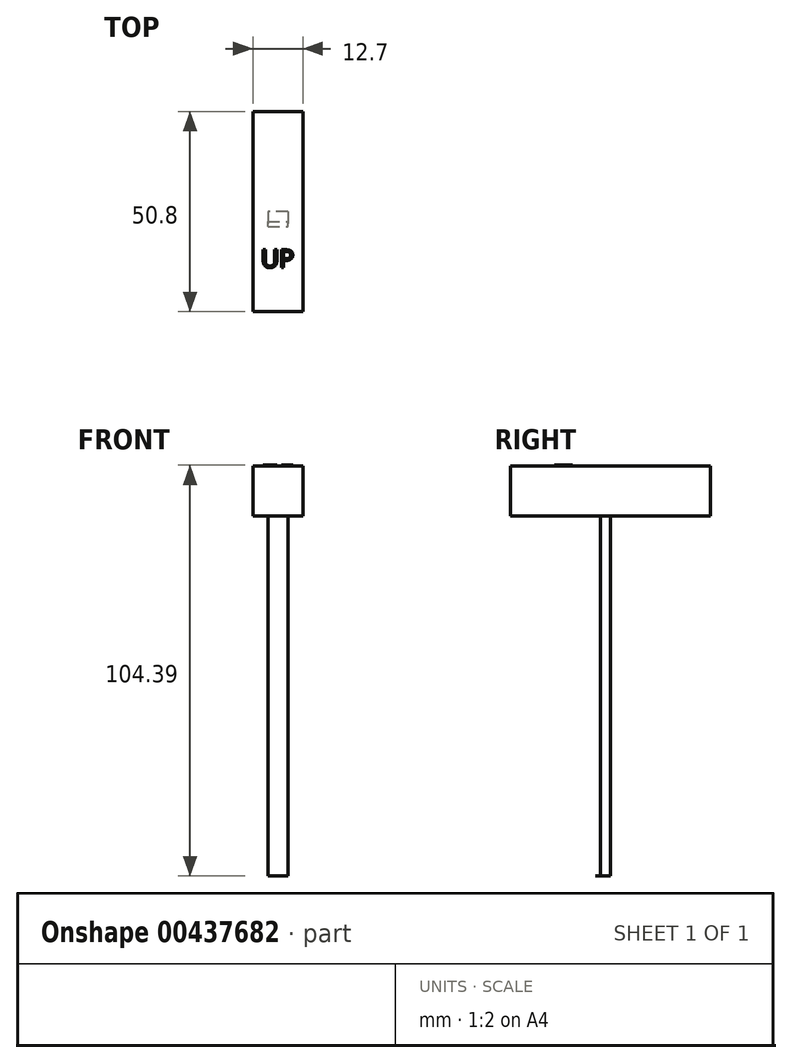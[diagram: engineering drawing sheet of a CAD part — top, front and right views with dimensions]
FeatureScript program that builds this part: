
annotation { "Feature Type Name" : "Feature", "Feature Type Description" : "" }
export const myFeature = defineFeature(function(context is Context, id is Id, definition is map)
    precondition{}
    {
        {
            var Q0;
            Q0=qCreatedBy(makeId("Front.planeOp"),FACE);
            var sketch = newSketch(context, id + "F0", { "sketchPlane" : qUnion([Q0])});
            skLineSegment(sketch, "E0.bottom", {"start": v(-6.35, 6.35) * mm, "end": v(6.35, 6.35) * mm});
            skLineSegment(sketch, "E0.top", {"start": v(-6.35, -6.35) * mm, "end": v(6.35, -6.35) * mm});
            skLineSegment(sketch, "E0.left", {"start": v(-6.35, 6.35) * mm, "end": v(-6.35, -6.35) * mm});
            skLineSegment(sketch, "E0.right", {"start": v(6.35, 6.35) * mm, "end": v(6.35, -6.35) * mm});
            skPoint(sketch, "E0.middle", {"position": v(0, 0) * mm});
            skSolve(sketch);
        }
        {
            var Q0;
            Q0=makeQuery(id+"F0.imprint","IMPRINT",FACE,{"disambiguationData":[TD([[makeQuery(id+"F0.imprint","IMPRINT",EDGE,{"derivedFrom":sQuery(id+"F0.wireOp",EDGE,"E0.bottom")}),-1.0]])]});
            extrude(context, id + "F1", {"entities" : qUnion([Q0]), "oppositeDirection" : true, "depth" : 50.8 * mm});
        }
        {
            var Q0;
            Q0=makeQuery(id+"F1.opExtrude","SWEPT_FACE",FACE,{"disambiguationData":[OSD([sQuery(id+"F0.wireOp",EDGE,"E0.right")])]});
            var sketch = newSketch(context, id + "F2", { "sketchPlane" : qUnion([Q0])});
            skLineSegment(sketch, "E1.bottom", {"start": v(25.4, 0) * mm, "end": v(-25.4, 0) * mm});
            skLineSegment(sketch, "E1.top", {"start": v(25.4, 12.7) * mm, "end": v(-25.4, 12.7) * mm});
            skLineSegment(sketch, "E1.left", {"start": v(25.4, 0) * mm, "end": v(25.4, 12.7) * mm});
            skLineSegment(sketch, "E1.right", {"start": v(-25.4, 0) * mm, "end": v(-25.4, 12.7) * mm});
            skPoint(sketch, "E1.middle", {"position": v(0, 6.35) * mm});
            skSolve(sketch);
        }
        {
            var Q0;
            {var subQ2=sQuery(id+"F2.wireOp",EDGE,"E1.top");Q0=makeQuery(id+"F2.imprint","IMPRINT",FACE,{"disambiguationData":[TD([[makeQuery(id+"F2.imprint","IMPRINT",EDGE,{"derivedFrom":subQ2}),1.0]])]});}
            var Q1;
            {var subQ0=sQuery(id+"F2.wireOp",EDGE,"E1.left");var subQ1=sQuery(id+"F2.wireOp",EDGE,"E1.bottom");var subQ2=makeQuery(id+"F2.imprint","INTERSECT",VERTEX,{"derivedFrom":[subQ1,subQ0]});Q1=makeQuery(id+"F2.imprint","IMPRINT",FACE,{"disambiguationData":[TD([[makeQuery(id+"F2.imprint","IMPRINT",EDGE,{"disambiguationData":[TD([[subQ2,-1.0]])],"derivedFrom":subQ1}),-1.0]])]});}
            extrude(context, id + "F3", {"entities" : qUnion([Q0, Q1]), "operationType" : NewBodyOperationType.REMOVE, "oppositeDirection" : true, "depth" : 25.4 * mm});
        }
        {
            var Q0;
            Q0=makeQuery(id+"F3.boolean.opBoolean","COPY",FACE,{"derivedFrom":makeQuery(id+"F3.opExtrude","SWEPT_FACE",FACE,{"disambiguationData":[OSD([sQuery(id+"F2.wireOp",EDGE,"E1.bottom")])]})});
            var sketch = newSketch(context, id + "F4", { "sketchPlane" : qUnion([Q0])});
            skLineSegment(sketch, "E2.bottom", {"start": v(-2.54, 22.86) * mm, "end": v(2.54, 22.86) * mm});
            skLineSegment(sketch, "E2.top", {"start": v(-2.54, 27.94) * mm, "end": v(2.54, 27.94) * mm});
            skLineSegment(sketch, "E2.left", {"start": v(-2.54, 22.86) * mm, "end": v(-2.54, 27.94) * mm});
            skLineSegment(sketch, "E2.right", {"start": v(2.54, 22.86) * mm, "end": v(2.54, 27.94) * mm});
            skPoint(sketch, "E2.middle", {"position": v(0, 25.4) * mm});
            skSolve(sketch);
        }
        {
            var Q0;
            {var subQ0=sQuery(id+"F4.wireOp",EDGE,"E2.bottom");Q0=makeQuery(id+"F4.imprint","IMPRINT",FACE,{"disambiguationData":[TD([[makeQuery(id+"F4.imprint","IMPRINT",EDGE,{"derivedFrom":subQ0}),1.0]])]});}
            extrude(context, id + "F5", {"entities" : qUnion([Q0]), "operationType" : NewBodyOperationType.REMOVE, "oppositeDirection" : true, "depth" : 25.4 * mm});
        }
        {
            var Q0;
            Q0=makeQuery(id+"F1.opExtrude","SWEPT_FACE",FACE,{"disambiguationData":[OSD([sQuery(id+"F0.wireOp",EDGE,"E0.right")])]});
            var sketch = newSketch(context, id + "F6", { "sketchPlane" : qUnion([Q0])});
            skLineSegment(sketch, "E3.bottom", {"start": v(25.4, 0) * mm, "end": v(0, 0) * mm});
            skLineSegment(sketch, "E3.top", {"start": v(25.4, 6.35) * mm, "end": v(0, 6.35) * mm});
            skLineSegment(sketch, "E3.left", {"start": v(25.4, 0) * mm, "end": v(25.4, 6.35) * mm});
            skLineSegment(sketch, "E3.right", {"start": v(0, 0) * mm, "end": v(0, 6.35) * mm});
            skSolve(sketch);
        }
        {
            var Q0;
            Q0=makeQuery(id+"F6.imprint","IMPRINT",FACE,{"disambiguationData":[TD([[makeQuery(id+"F6.imprint","IMPRINT",EDGE,{"derivedFrom":sQuery(id+"F6.wireOp",EDGE,"E3.bottom")}),-1.0]])]});
            extrude(context, id + "F7", {"entities" : qUnion([Q0]), "oppositeDirection" : true, "depth" : 12.7 * mm});
        }
        {
            var Q0;
            Q0=makeQuery(id+"F7.opExtrude","SWEPT_FACE",FACE,{"disambiguationData":[OSD([sQuery(id+"F6.wireOp",EDGE,"E3.bottom")])]});
            var sketch = newSketch(context, id + "F8", { "sketchPlane" : qUnion([Q0])});
            skLineSegment(sketch, "E4.bottom", {"start": v(-2.54, -25.4) * mm, "end": v(2.54, -25.4) * mm});
            skLineSegment(sketch, "E4.top", {"start": v(-2.54, -22.86) * mm, "end": v(2.54, -22.86) * mm});
            skLineSegment(sketch, "E4.left", {"start": v(-2.54, -25.4) * mm, "end": v(-2.54, -22.86) * mm});
            skLineSegment(sketch, "E4.right", {"start": v(2.54, -25.4) * mm, "end": v(2.54, -22.86) * mm});
            skLineSegment(sketch, "E5.top", {"start": v(-1.27, -25.4) * mm, "end": v(1.27, -25.4) * mm});
            skPoint(sketch, "E5.middle", {"position": v(0, -22.86) * mm});
            skSolve(sketch);
        }
        {
            var Q0;
            Q0=makeQuery(id+"F8.imprint","IMPRINT",FACE,{"disambiguationData":[TD([[makeQuery(id+"F8.imprint","IMPRINT",EDGE,{"derivedFrom":sQuery(id+"F8.wireOp",EDGE,"E4.bottom")}),1.0]])]});
            extrude(context, id + "F9", {"entities" : qUnion([Q0]), "operationType" : NewBodyOperationType.ADD, "depth" : 97.8 * mm});
        }
        {
            var Q0;
            Q0=makeQuery(id+"F9.opExtrude","CAP_FACE",FACE,{"disambiguationData":[OSD([sQuery(id+"F8.wireOp",EDGE,"E4.bottom"),sQuery(id+"F8.wireOp",EDGE,"E4.top"),sQuery(id+"F8.wireOp",EDGE,"E4.left"),sQuery(id+"F8.wireOp",EDGE,"E4.right"),sQuery(id+"F8.wireOp",EDGE,"E5.top")])],"isStart":false});
            var sketch = newSketch(context, id + "F10", { "sketchPlane" : qUnion([Q0])});
            skLineSegment(sketch, "E6.bottom", {"start": v(-2.54, -21.6) * mm, "end": v(2.54, -21.6) * mm});
            skLineSegment(sketch, "E6.top", {"start": v(-2.54, -24) * mm, "end": v(2.54, -24) * mm});
            skLineSegment(sketch, "E6.left", {"start": v(-2.54, -21.6) * mm, "end": v(-2.54, -24) * mm});
            skLineSegment(sketch, "E6.right", {"start": v(2.54, -21.6) * mm, "end": v(2.54, -24) * mm});
            skPoint(sketch, "E6.middle", {"position": v(0, -22.8) * mm});
            skPoint(sketch, "E6.middle.positionSnap0", {"position": v(0, -22.86) * mm});
            skPoint(sketch, "E6.centerSnap0", {"position": v(0, -22.86) * mm});
            skSolve(sketch);
        }
        {
            var Q0;
            {var subQ0=sQuery(id+"F10.wireOp",EDGE,"E6.bottom");Q0=makeQuery(id+"F10.imprint","IMPRINT",FACE,{"disambiguationData":[TD([[makeQuery(id+"F10.imprint","IMPRINT",EDGE,{"derivedFrom":subQ0}),-1.0]])]});}
            extrude(context, id + "F11", {"entities" : qUnion([Q0]), "operationType" : NewBodyOperationType.ADD, "oppositeDirection" : true, "depth" : 0.03 * mm});
        }
        {
            var Q0;
            Q0=makeQuery(id+"F7.opExtrude","SWEPT_FACE",FACE,{"disambiguationData":[OSD([sQuery(id+"F6.wireOp",EDGE,"E3.top")])]});
            var sketch = newSketch(context, id + "F12", { "sketchPlane" : qUnion([Q0])});
            skText(sketch, "E7", { "text": "UP\n", "fontName": "OpenSans-Regular.ttf"});
            const initialGuessF12  = {"E7": [-0.0043, 0.0112, 1, 0, 0.00455]};
            skSetInitialGuess(sketch, initialGuessF12);
            skSolve(sketch);
        }
        {
            var Q0;
            Q0 = qSketchRegion(id + "F12", true);
            extrude(context, id + "F13", {"entities" : qUnion([Q0]), "operationType" : NewBodyOperationType.ADD, "depth" : 0.25 * mm});
        }
    });
